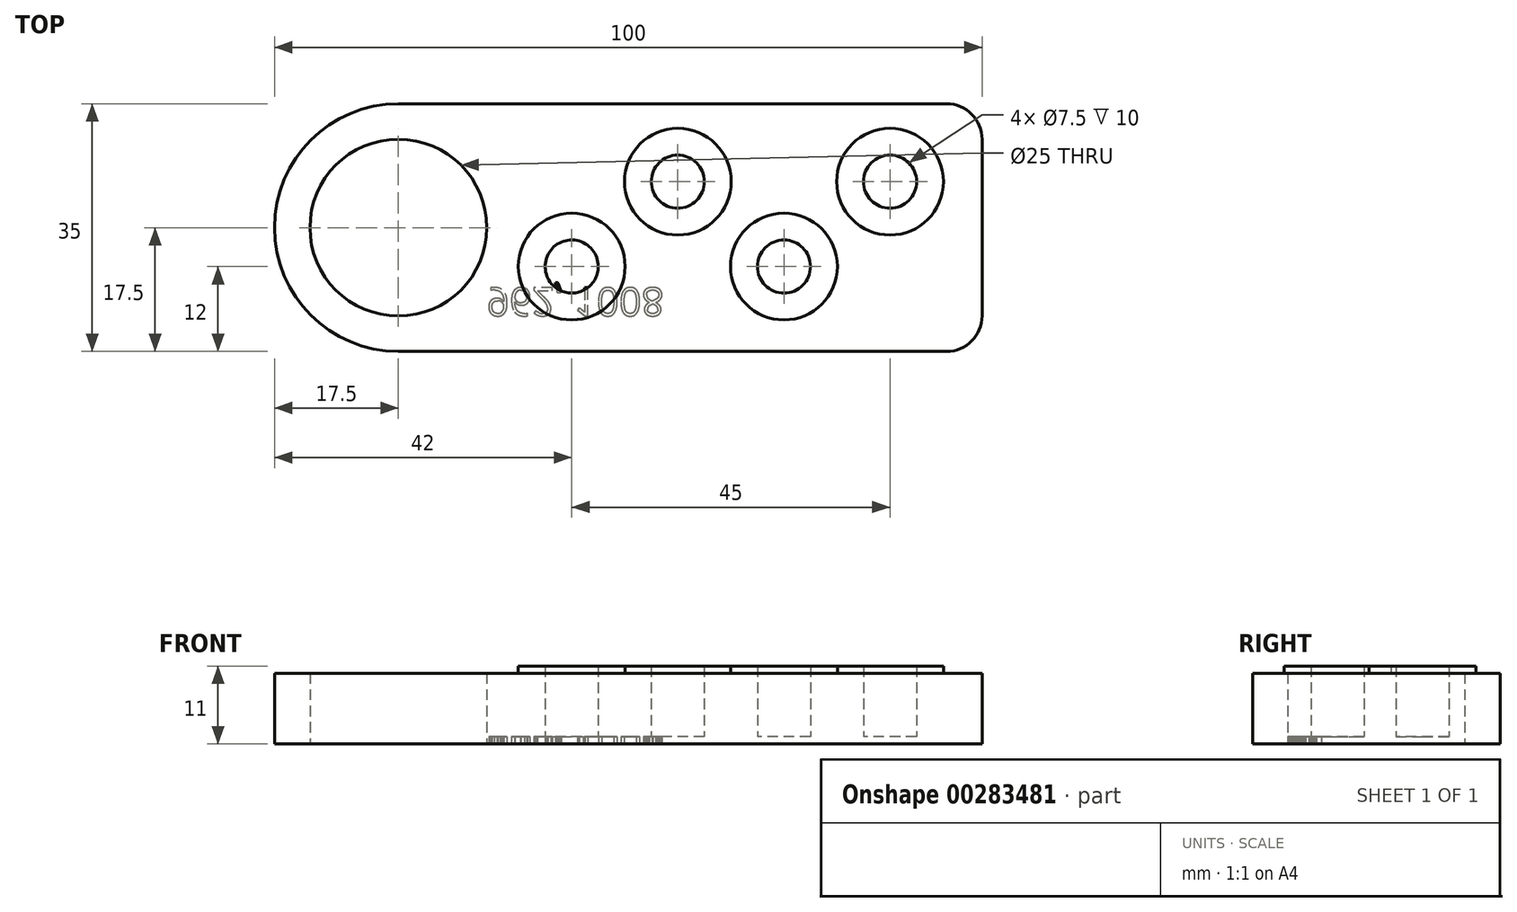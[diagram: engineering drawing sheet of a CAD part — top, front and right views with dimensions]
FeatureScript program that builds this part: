
annotation { "Feature Type Name" : "Feature", "Feature Type Description" : "" }
export const myFeature = defineFeature(function(context is Context, id is Id, definition is map)
    precondition{}
    {
        {
            var Q0;
            Q0=qCreatedBy(makeId("Top.planeOp"),FACE);
            var sketch = newSketch(context, id + "F0", { "sketchPlane" : qUnion([Q0])});
            skLineSegment(sketch, "E0.bottom", {"start": v(17.5, 0) * mm, "end": v(95, 0) * mm});
            skLineSegment(sketch, "E0.top", {"start": v(17.5, 35) * mm, "end": v(95, 35) * mm});
            skLineSegment(sketch, "E0.left", {"start": v(0, 17.5) * mm, "end": v(0, 17.5) * mm});
            skLineSegment(sketch, "E0.right", {"start": v(100, 5) * mm, "end": v(100, 30) * mm});
            skLineSegment(sketch, "E1.bottom", {"start": v(0, 0) * mm, "end": v(17.5, 0) * mm, "construction": true});
            skLineSegment(sketch, "E1.top", {"start": v(0, 17.5) * mm, "end": v(17.5, 17.5) * mm, "construction": true});
            skLineSegment(sketch, "E1.left", {"start": v(0, 0) * mm, "end": v(0, 17.5) * mm, "construction": true});
            skLineSegment(sketch, "E1.right", {"start": v(17.5, 0) * mm, "end": v(17.5, 17.5) * mm, "construction": true});
            skCircle(sketch, "E2", {"center": v(17.5, 17.5) * mm, "radius": 12.5 * mm});
            skPoint(sketch, "E3.visualSharp", {"position": v(0, 0) * mm});
            skArc(sketch, "E3.filletArc", {"start": v(0, 17.5) * mm, "mid": v(5.13, 5.13) * mm, "end": v(17.5, 0) * mm});
            skPoint(sketch, "E4.visualSharp", {"position": v(0, 35) * mm});
            skArc(sketch, "E4.filletArc", {"start": v(17.5, 35) * mm, "mid": v(5.13, 29.87) * mm, "end": v(0, 17.5) * mm});
            skPoint(sketch, "E5.visualSharp", {"position": v(100, 35) * mm});
            skArc(sketch, "E5.filletArc", {"start": v(100, 30) * mm, "mid": v(98.54, 33.54) * mm, "end": v(95, 35) * mm});
            skPoint(sketch, "E6.visualSharp", {"position": v(100, 0) * mm});
            skArc(sketch, "E6.filletArc", {"start": v(95, 0) * mm, "mid": v(98.54, 1.46) * mm, "end": v(100, 5) * mm});
            skSolve(sketch);
        }
        {
            var Q0;
            Q0=makeQuery(id+"F0.imprint","IMPRINT",FACE,{"disambiguationData":[TD([[makeQuery(id+"F0.imprint","IMPRINT",EDGE,{"derivedFrom":sQuery(id+"F0.wireOp",EDGE,"E0.bottom")}),1.0]])]});
            extrude(context, id + "F1", {"entities" : qUnion([Q0]), "depth" : 10 * mm});
        }
        {
            var Q0;
            Q0=makeQuery(id+"F1.opExtrude","CAP_FACE",FACE,{"disambiguationData":[OSD([sQuery(id+"F0.wireOp",EDGE,"E0.bottom"),sQuery(id+"F0.wireOp",EDGE,"E0.top"),sQuery(id+"F0.wireOp",EDGE,"E0.right"),sQuery(id+"F0.wireOp",EDGE,"E2"),sQuery(id+"F0.wireOp",EDGE,"E3.filletArc"),sQuery(id+"F0.wireOp",EDGE,"E4.filletArc"),sQuery(id+"F0.wireOp",EDGE,"E5.filletArc"),sQuery(id+"F0.wireOp",EDGE,"E6.filletArc")])],"isStart":false});
            var sketch = newSketch(context, id + "F2", { "sketchPlane" : qUnion([Q0])});
            skLineSegment(sketch, "E7.bottom", {"start": v(0, 0) * mm, "end": v(42, 0) * mm, "construction": true});
            skLineSegment(sketch, "E7.top", {"start": v(0, 12) * mm, "end": v(42, 12) * mm, "construction": true});
            skLineSegment(sketch, "E7.left", {"start": v(0, 0) * mm, "end": v(0, 12) * mm, "construction": true});
            skLineSegment(sketch, "E7.right", {"start": v(42, 0) * mm, "end": v(42, 12) * mm, "construction": true});
            skCircle(sketch, "E8", {"center": v(42, 12) * mm, "radius": 7.55 * mm});
            skLineSegment(sketch, "E9.bottom", {"start": v(42, 12) * mm, "end": v(57, 12) * mm, "construction": true});
            skLineSegment(sketch, "E9.top", {"start": v(42, 24) * mm, "end": v(57, 24) * mm, "construction": true});
            skLineSegment(sketch, "E9.left", {"start": v(42, 12) * mm, "end": v(42, 24) * mm, "construction": true});
            skLineSegment(sketch, "E9.right", {"start": v(57, 12) * mm, "end": v(57, 24) * mm, "construction": true});
            skCircle(sketch, "E10", {"center": v(57, 24) * mm, "radius": 7.55 * mm});
            skLineSegment(sketch, "E11.bottom", {"start": v(57, 24) * mm, "end": v(72, 24) * mm, "construction": true});
            skLineSegment(sketch, "E11.top", {"start": v(57, 12) * mm, "end": v(72, 12) * mm, "construction": true});
            skLineSegment(sketch, "E11.left", {"start": v(57, 24) * mm, "end": v(57, 12) * mm, "construction": true});
            skLineSegment(sketch, "E11.right", {"start": v(72, 24) * mm, "end": v(72, 12) * mm, "construction": true});
            skLineSegment(sketch, "E12.bottom", {"start": v(72, 12) * mm, "end": v(87, 12) * mm, "construction": true});
            skLineSegment(sketch, "E12.top", {"start": v(72, 24) * mm, "end": v(87, 24) * mm, "construction": true});
            skLineSegment(sketch, "E12.left", {"start": v(72, 12) * mm, "end": v(72, 24) * mm, "construction": true});
            skLineSegment(sketch, "E12.right", {"start": v(87, 12) * mm, "end": v(87, 24) * mm, "construction": true});
            skCircle(sketch, "E13", {"center": v(72, 12) * mm, "radius": 7.55 * mm});
            skCircle(sketch, "E14", {"center": v(87, 24) * mm, "radius": 7.55 * mm});
            skCircle(sketch, "E15", {"center": v(87, 24) * mm, "radius": 3.75 * mm});
            skCircle(sketch, "E16", {"center": v(57, 24) * mm, "radius": 3.75 * mm});
            skCircle(sketch, "E17", {"center": v(72, 12) * mm, "radius": 3.75 * mm});
            skCircle(sketch, "E18", {"center": v(42, 12) * mm, "radius": 3.75 * mm});
            skSolve(sketch);
        }
        {
            var Q0;
            Q0=makeQuery(id+"F2.imprint","IMPRINT",FACE,{"disambiguationData":[TD([[makeQuery(id+"F2.imprint","IMPRINT",EDGE,{"derivedFrom":sQuery(id+"F2.wireOp",EDGE,"E8")}),1.0]])]});
            var Q1;
            Q1=makeQuery(id+"F2.imprint","IMPRINT",FACE,{"disambiguationData":[TD([[makeQuery(id+"F2.imprint","IMPRINT",EDGE,{"derivedFrom":sQuery(id+"F2.wireOp",EDGE,"E10")}),1.0]])]});
            var Q2;
            Q2=makeQuery(id+"F2.imprint","IMPRINT",FACE,{"disambiguationData":[TD([[makeQuery(id+"F2.imprint","IMPRINT",EDGE,{"derivedFrom":sQuery(id+"F2.wireOp",EDGE,"E13")}),1.0]])]});
            var Q3;
            Q3=makeQuery(id+"F2.imprint","IMPRINT",FACE,{"disambiguationData":[TD([[makeQuery(id+"F2.imprint","IMPRINT",EDGE,{"derivedFrom":sQuery(id+"F2.wireOp",EDGE,"E14")}),1.0]])]});
            extrude(context, id + "F3", {"entities" : qUnion([Q0, Q1, Q2, Q3]), "operationType" : NewBodyOperationType.ADD, "depth" : 1 * mm});
        }
        {
            var Q0;
            Q0=makeQuery(id+"F3.boolean.opBoolean","SPLIT",FACE,{"disambiguationData":[TD([makeQuery(id+"F3.opExtrude","SWEPT_FACE",FACE,{"disambiguationData":[OSD([sQuery(id+"F2.wireOp",EDGE,"E18")])]})])],"derivedFrom":makeQuery(id+"F1.opExtrude","CAP_FACE",FACE,{"disambiguationData":[OSD([sQuery(id+"F0.wireOp",EDGE,"E0.bottom"),sQuery(id+"F0.wireOp",EDGE,"E0.top"),sQuery(id+"F0.wireOp",EDGE,"E0.right"),sQuery(id+"F0.wireOp",EDGE,"E2"),sQuery(id+"F0.wireOp",EDGE,"E3.filletArc"),sQuery(id+"F0.wireOp",EDGE,"E4.filletArc"),sQuery(id+"F0.wireOp",EDGE,"E5.filletArc"),sQuery(id+"F0.wireOp",EDGE,"E6.filletArc")])],"isStart":false})});
            var Q1;
            Q1=makeQuery(id+"F3.boolean.opBoolean","SPLIT",FACE,{"disambiguationData":[TD([makeQuery(id+"F3.opExtrude","SWEPT_FACE",FACE,{"disambiguationData":[OSD([sQuery(id+"F2.wireOp",EDGE,"E16")])]})])],"derivedFrom":makeQuery(id+"F1.opExtrude","CAP_FACE",FACE,{"disambiguationData":[OSD([sQuery(id+"F0.wireOp",EDGE,"E0.bottom"),sQuery(id+"F0.wireOp",EDGE,"E0.top"),sQuery(id+"F0.wireOp",EDGE,"E0.right"),sQuery(id+"F0.wireOp",EDGE,"E2"),sQuery(id+"F0.wireOp",EDGE,"E3.filletArc"),sQuery(id+"F0.wireOp",EDGE,"E4.filletArc"),sQuery(id+"F0.wireOp",EDGE,"E5.filletArc"),sQuery(id+"F0.wireOp",EDGE,"E6.filletArc")])],"isStart":false})});
            var Q2;
            Q2=makeQuery(id+"F3.boolean.opBoolean","SPLIT",FACE,{"disambiguationData":[TD([makeQuery(id+"F3.opExtrude","SWEPT_FACE",FACE,{"disambiguationData":[OSD([sQuery(id+"F2.wireOp",EDGE,"E17")])]})])],"derivedFrom":makeQuery(id+"F1.opExtrude","CAP_FACE",FACE,{"disambiguationData":[OSD([sQuery(id+"F0.wireOp",EDGE,"E0.bottom"),sQuery(id+"F0.wireOp",EDGE,"E0.top"),sQuery(id+"F0.wireOp",EDGE,"E0.right"),sQuery(id+"F0.wireOp",EDGE,"E2"),sQuery(id+"F0.wireOp",EDGE,"E3.filletArc"),sQuery(id+"F0.wireOp",EDGE,"E4.filletArc"),sQuery(id+"F0.wireOp",EDGE,"E5.filletArc"),sQuery(id+"F0.wireOp",EDGE,"E6.filletArc")])],"isStart":false})});
            var Q3;
            Q3=makeQuery(id+"F3.boolean.opBoolean","SPLIT",FACE,{"disambiguationData":[TD([makeQuery(id+"F3.opExtrude","SWEPT_FACE",FACE,{"disambiguationData":[OSD([sQuery(id+"F2.wireOp",EDGE,"E15")])]})])],"derivedFrom":makeQuery(id+"F1.opExtrude","CAP_FACE",FACE,{"disambiguationData":[OSD([sQuery(id+"F0.wireOp",EDGE,"E0.bottom"),sQuery(id+"F0.wireOp",EDGE,"E0.top"),sQuery(id+"F0.wireOp",EDGE,"E0.right"),sQuery(id+"F0.wireOp",EDGE,"E2"),sQuery(id+"F0.wireOp",EDGE,"E3.filletArc"),sQuery(id+"F0.wireOp",EDGE,"E4.filletArc"),sQuery(id+"F0.wireOp",EDGE,"E5.filletArc"),sQuery(id+"F0.wireOp",EDGE,"E6.filletArc")])],"isStart":false})});
            extrude(context, id + "F4", {"entities" : qUnion([Q0, Q1, Q2, Q3]), "operationType" : NewBodyOperationType.REMOVE, "oppositeDirection" : true, "depth" : 9 * mm});
        }
        {
            var Q0;
            Q0=makeQuery(id+"F1.opExtrude","CAP_FACE",FACE,{"disambiguationData":[OSD([sQuery(id+"F0.wireOp",EDGE,"E0.bottom"),sQuery(id+"F0.wireOp",EDGE,"E0.top"),sQuery(id+"F0.wireOp",EDGE,"E0.right"),sQuery(id+"F0.wireOp",EDGE,"E2"),sQuery(id+"F0.wireOp",EDGE,"E3.filletArc"),sQuery(id+"F0.wireOp",EDGE,"E4.filletArc"),sQuery(id+"F0.wireOp",EDGE,"E5.filletArc"),sQuery(id+"F0.wireOp",EDGE,"E6.filletArc")])],"isStart":true});
            var sketch = newSketch(context, id + "F5", { "sketchPlane" : qUnion([Q0])});
            skLineSegment(sketch, "E19.bottom", {"start": v(0, 0) * mm, "end": v(30, 0) * mm, "construction": true});
            skLineSegment(sketch, "E19.top", {"start": v(0, -5) * mm, "end": v(30, -5) * mm, "construction": true});
            skLineSegment(sketch, "E19.left", {"start": v(0, 0) * mm, "end": v(0, -5) * mm, "construction": true});
            skLineSegment(sketch, "E19.right", {"start": v(30, 0) * mm, "end": v(30, -5) * mm, "construction": true});
            skText(sketch, "E20", { "text": "962, 1008", "fontName": "OpenSans-Regular.ttf"});
            const initialGuessF5  = {"E20": [0.03, -0.009, 1, 0, 0.004]};
            skSetInitialGuess(sketch, initialGuessF5);
            skSolve(sketch);
        }
        {
            var Q0;
            Q0 = qSketchRegion(id + "F5", true);
            extrude(context, id + "F6", {"entities" : qUnion([Q0]), "operationType" : NewBodyOperationType.REMOVE, "oppositeDirection" : true, "depth" : 1 * mm});
        }
    });
